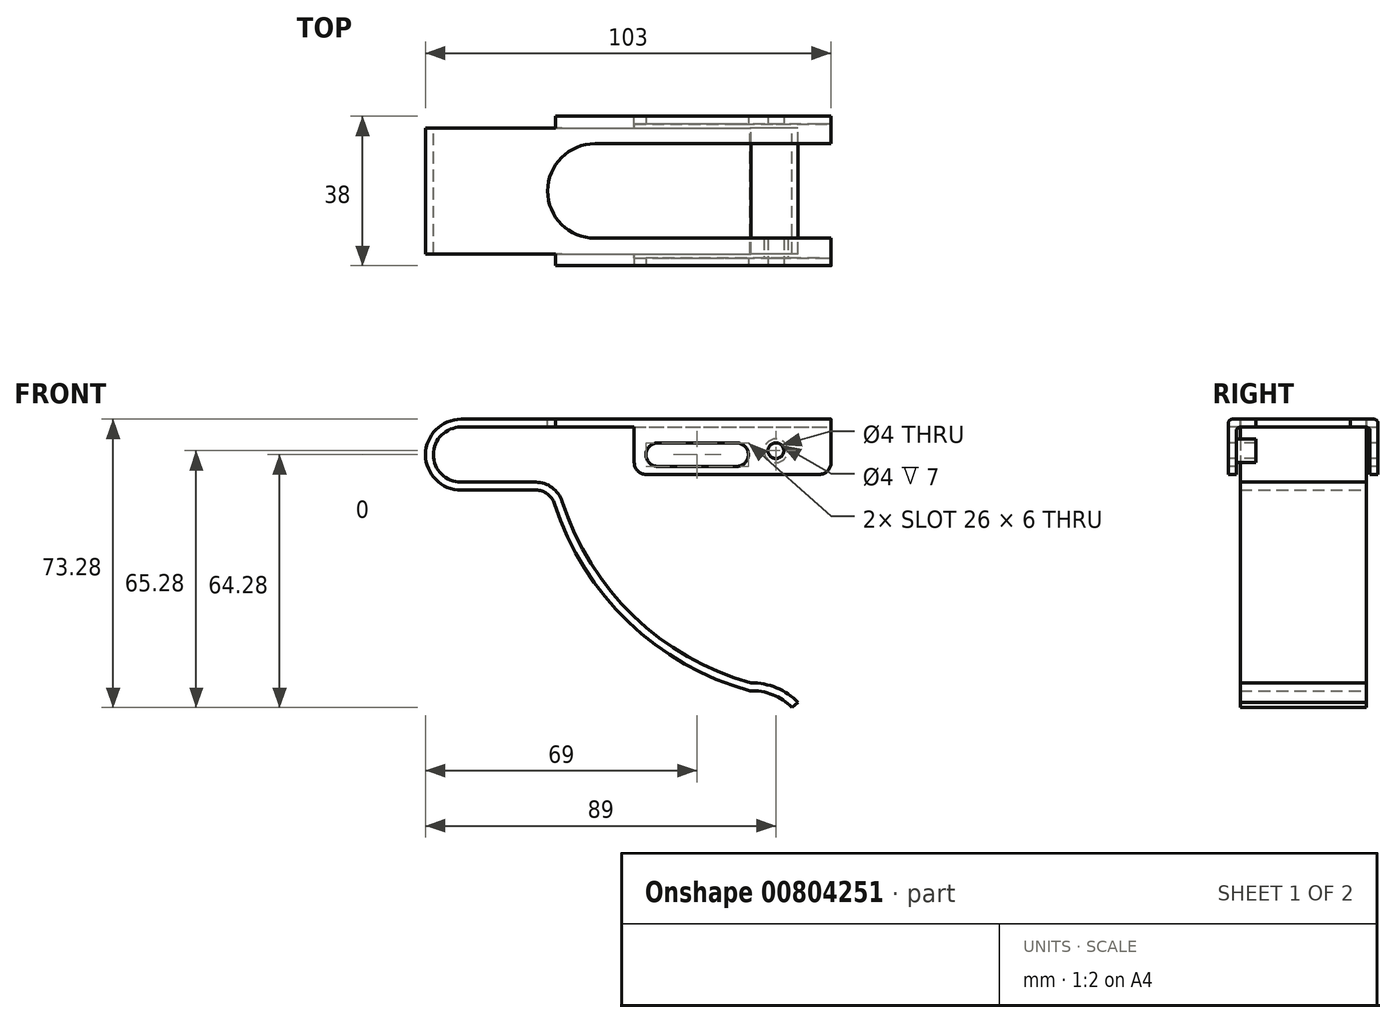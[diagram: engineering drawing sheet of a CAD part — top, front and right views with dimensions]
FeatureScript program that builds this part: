
annotation { "Feature Type Name" : "Feature", "Feature Type Description" : "" }
export const myFeature = defineFeature(function(context is Context, id is Id, definition is map)
    precondition{}
    {
        {
            var Q0;
            Q0=qCreatedBy(makeId("Front.planeOp"),FACE);
            var sketch = newSketch(context, id + "F0", { "sketchPlane" : qUnion([Q0])});
            skArc(sketch, "E0", {"start": v(0, 9) * mm, "mid": v(-9, 0) * mm, "end": v(0, -9) * mm});
            skLineSegment(sketch, "E1", {"start": v(0, 9) * mm, "end": v(94, 9) * mm});
            skLineSegment(sketch, "E2", {"start": v(0, -9) * mm, "end": v(19, -9) * mm});
            skArc(sketch, "E3", {"start": v(23.76, -12.48) * mm, "mid": v(42.54, -42.55) * mm, "end": v(73.4, -60) * mm});
            skArc(sketch, "E4", {"start": v(84.1, -64.28) * mm, "mid": v(79.2, -61) * mm, "end": v(73.4, -60) * mm});
            skPoint(sketch, "E5.visualSharp", {"position": v(22.75, -9) * mm});
            skArc(sketch, "E5.filletArc", {"start": v(23.76, -12.48) * mm, "mid": v(21.95, -9.96) * mm, "end": v(19, -9) * mm});
            skLineSegment(sketch, "E6.0", {"start": v(0, 7) * mm, "end": v(94, 7) * mm});
            skArc(sketch, "E6.1", {"start": v(0, 7) * mm, "mid": v(-7, 0) * mm, "end": v(0, -7) * mm});
            skArc(sketch, "E6.2", {"start": v(85.63, -63) * mm, "mid": v(80.16, -59.23) * mm, "end": v(73.63, -58) * mm});
            skArc(sketch, "E6.3", {"start": v(25.67, -11.87) * mm, "mid": v(43.82, -41) * mm, "end": v(73.63, -58) * mm});
            skArc(sketch, "E6.4", {"start": v(25.67, -11.87) * mm, "mid": v(23.13, -8.35) * mm, "end": v(19, -7) * mm});
            skLineSegment(sketch, "E6.5", {"start": v(0, -7) * mm, "end": v(19, -7) * mm});
            skLineSegment(sketch, "E7", {"start": v(94, 9) * mm, "end": v(94, 7) * mm});
            skLineSegment(sketch, "E8", {"start": v(85.63, -63) * mm, "end": v(84.1, -64.28) * mm});
            skSolve(sketch);
        }
        {
            var Q0;
            Q0 = qSketchRegion(id + "F0", true);
            extrude(context, id + "F1", {"entities" : qUnion([Q0]), "depth" : 16 * mm, "offsetDistance" : 25 * mm});
        }
        {
            var Q0;
            Q0=makeQuery(id+"F1.opExtrude","SWEPT_FACE",FACE,{"disambiguationData":[OSD([sQuery(id+"F0.wireOp",EDGE,"E1")])]});
            var sketch = newSketch(context, id + "F2", { "sketchPlane" : qUnion([Q0])});
            skLineSegment(sketch, "E9.bottom", {"start": v(94, -16) * mm, "end": v(24, -16) * mm});
            skLineSegment(sketch, "E9.top", {"start": v(94, -19) * mm, "end": v(24, -19) * mm});
            skLineSegment(sketch, "E9.left", {"start": v(94, -16) * mm, "end": v(94, -19) * mm});
            skLineSegment(sketch, "E9.right", {"start": v(24, -16) * mm, "end": v(24, -19) * mm});
            skSolve(sketch);
        }
        {
            var Q0;
            Q0=makeQuery(id+"F2.imprint","IMPRINT",FACE,{"disambiguationData":[TD([[makeQuery(id+"F2.imprint","IMPRINT",EDGE,{"derivedFrom":sQuery(id+"F2.wireOp",EDGE,"E9.bottom")}),-1.0]])]});
            extrude(context, id + "F3", {"entities" : qUnion([Q0]), "operationType" : NewBodyOperationType.ADD, "oppositeDirection" : true, "depth" : 2 * mm, "offsetDistance" : 25 * mm});
        }
        {
            var Q0;
            Q0=makeQuery(id+"F3.opExtrude","SWEPT_FACE",FACE,{"disambiguationData":[OSD([sQuery(id+"F2.wireOp",EDGE,"E9.top")])]});
            var sketch = newSketch(context, id + "F4", { "sketchPlane" : qUnion([Q0])});
            skLineSegment(sketch, "E10.bottom", {"start": v(94, 9) * mm, "end": v(44, 9) * mm});
            skLineSegment(sketch, "E10.top", {"start": v(94, -5) * mm, "end": v(44, -5) * mm});
            skLineSegment(sketch, "E10.left", {"start": v(94, 9) * mm, "end": v(94, -5) * mm});
            skLineSegment(sketch, "E10.right", {"start": v(44, 9) * mm, "end": v(44, -5) * mm});
            skSolve(sketch);
        }
        {
            var Q0;
            Q0 = qSketchRegion(id + "F4", true);
            extrude(context, id + "F5", {"entities" : qUnion([Q0]), "operationType" : NewBodyOperationType.ADD, "oppositeDirection" : true, "depth" : 2 * mm, "offsetDistance" : 25 * mm});
        }
        {
            var Q0;
            Q0=makeQuery(id+"F5.boolean.opBoolean","INTERSECT",EDGE,{"derivedFrom":[makeQuery(id+"F3.boolean.opBoolean","MERGE",FACE,{"derivedFrom":[makeQuery(id+"F1.opExtrude","SWEPT_FACE",FACE,{"disambiguationData":[OSD([sQuery(id+"F0.wireOp",EDGE,"E6.0")])]}),makeQuery(id+"F3.opExtrude","CAP_FACE",FACE,{"disambiguationData":[OSD([sQuery(id+"F2.wireOp",EDGE,"E9.bottom"),sQuery(id+"F2.wireOp",EDGE,"E9.top"),sQuery(id+"F2.wireOp",EDGE,"E9.left"),sQuery(id+"F2.wireOp",EDGE,"E9.right")])],"isStart":false})]}),makeQuery(id+"F5.opExtrude","CAP_FACE",FACE,{"disambiguationData":[OSD([sQuery(id+"F4.wireOp",EDGE,"E10.bottom"),sQuery(id+"F4.wireOp",EDGE,"E10.top"),sQuery(id+"F4.wireOp",EDGE,"E10.left"),sQuery(id+"F4.wireOp",EDGE,"E10.right")])],"isStart":false})]});
            var Q1;
            Q1=makeQuery(id+"F3.opExtrude","CAP_EDGE",EDGE,{"disambiguationData":[OSD([sQuery(id+"F2.wireOp",EDGE,"E9.top")])],"isStart":true});
            fillet(context, id + "F6", {"entities" : qUnion([Q0, Q1]), "radius" : 1 * mm, "tangentPropagation" : true, "allowEdgeOverflow" : false});
        }
        {
            var Q0;
            Q0=makeQuery(id+"F1.opExtrude","SWEPT_BODY",BODY,{"disambiguationData":[OSD([sQuery(id+"F0.wireOp",EDGE,"E0"),sQuery(id+"F0.wireOp",EDGE,"E1"),sQuery(id+"F0.wireOp",EDGE,"E2"),sQuery(id+"F0.wireOp",EDGE,"E3"),sQuery(id+"F0.wireOp",EDGE,"E4"),sQuery(id+"F0.wireOp",EDGE,"E5.filletArc"),sQuery(id+"F0.wireOp",EDGE,"E6.0"),sQuery(id+"F0.wireOp",EDGE,"E6.1"),sQuery(id+"F0.wireOp",EDGE,"E6.2"),sQuery(id+"F0.wireOp",EDGE,"E6.3"),sQuery(id+"F0.wireOp",EDGE,"E6.4"),sQuery(id+"F0.wireOp",EDGE,"E6.5"),sQuery(id+"F0.wireOp",EDGE,"E7"),sQuery(id+"F0.wireOp",EDGE,"E8")])]});
            var Q1;
            Q1=qCreatedBy(makeId("Front.planeOp"),FACE);
            mirror(context, id + "F7", {"operationType" : NewBodyOperationType.ADD, "entities" : qUnion([Q0]), "mirrorPlane" : qUnion([Q1])});
        }
        {
            var Q0;
            {var subQ0=makeQuery(id+"F3.boolean.opBoolean","MERGE",FACE,{"derivedFrom":[makeQuery(id+"F1.opExtrude","SWEPT_FACE",FACE,{"disambiguationData":[OSD([sQuery(id+"F0.wireOp",EDGE,"E1")])]}),makeQuery(id+"F3.opExtrude","CAP_FACE",FACE,{"disambiguationData":[OSD([sQuery(id+"F2.wireOp",EDGE,"E9.bottom"),sQuery(id+"F2.wireOp",EDGE,"E9.top"),sQuery(id+"F2.wireOp",EDGE,"E9.left"),sQuery(id+"F2.wireOp",EDGE,"E9.right")])],"isStart":true})]});Q0=makeQuery(id+"F7.boolean.opBoolean","MERGE",FACE,{"derivedFrom":[subQ0,makeQuery(id+"F7.opPattern","COPY",FACE,{"derivedFrom":subQ0,"instanceName":"1"})]});}
            var sketch = newSketch(context, id + "F8", { "sketchPlane" : qUnion([Q0])});
            skArc(sketch, "E11", {"start": v(34, 12) * mm, "mid": v(22, 0) * mm, "end": v(34, -12) * mm});
            skLineSegment(sketch, "E12", {"start": v(34, 12) * mm, "end": v(94, 12) * mm});
            skLineSegment(sketch, "E13", {"start": v(34, -12) * mm, "end": v(94, -12) * mm});
            skLineSegment(sketch, "E14", {"start": v(94, -12) * mm, "end": v(94, 12) * mm});
            skSolve(sketch);
        }
        {
            var Q0;
            Q0 = qSketchRegion(id + "F8", true);
            extrude(context, id + "F9", {"entities" : qUnion([Q0]), "operationType" : NewBodyOperationType.REMOVE, "oppositeDirection" : true, "depth" : 2 * mm, "offsetDistance" : 25 * mm});
        }
        {
            var Q0;
            Q0=makeQuery(id+"F5.boolean.opBoolean","MERGE",FACE,{"derivedFrom":[makeQuery(id+"F3.opExtrude","SWEPT_FACE",FACE,{"disambiguationData":[OSD([sQuery(id+"F2.wireOp",EDGE,"E9.top")])]}),makeQuery(id+"F5.opExtrude","CAP_FACE",FACE,{"disambiguationData":[OSD([sQuery(id+"F4.wireOp",EDGE,"E10.bottom"),sQuery(id+"F4.wireOp",EDGE,"E10.top"),sQuery(id+"F4.wireOp",EDGE,"E10.left"),sQuery(id+"F4.wireOp",EDGE,"E10.right")])],"isStart":true})]});
            var sketch = newSketch(context, id + "F10", { "sketchPlane" : qUnion([Q0])});
            skLineSegment(sketch, "E15", {"start": v(50, 0) * mm, "end": v(70, 0) * mm});
            skArc(sketch, "E16.0.startCap", {"start": v(50, -3) * mm, "mid": v(47, 0) * mm, "end": v(50, 3) * mm});
            skArc(sketch, "E16.0.endCap", {"start": v(70, 3) * mm, "mid": v(73, 0) * mm, "end": v(70, -3) * mm});
            skLineSegment(sketch, "E16.0.left", {"start": v(50, 3) * mm, "end": v(70, 3) * mm});
            skLineSegment(sketch, "E16.0.right", {"start": v(50, -3) * mm, "end": v(70, -3) * mm});
            skSolve(sketch);
        }
        {
            var Q0;
            Q0 = qSketchRegion(id + "F10", true);
            extrude(context, id + "F11", {"entities" : qUnion([Q0]), "operationType" : NewBodyOperationType.REMOVE, "endBound" : BoundingType.THROUGH_ALL, "oppositeDirection" : true, "depth" : 25 * mm, "offsetDistance" : 25 * mm});
        }
        {
            var Q0;
            Q0=makeQuery(id+"F5.boolean.opBoolean","MERGE",FACE,{"derivedFrom":[makeQuery(id+"F3.opExtrude","SWEPT_FACE",FACE,{"disambiguationData":[OSD([sQuery(id+"F2.wireOp",EDGE,"E9.top")])]}),makeQuery(id+"F5.opExtrude","CAP_FACE",FACE,{"disambiguationData":[OSD([sQuery(id+"F4.wireOp",EDGE,"E10.bottom"),sQuery(id+"F4.wireOp",EDGE,"E10.top"),sQuery(id+"F4.wireOp",EDGE,"E10.left"),sQuery(id+"F4.wireOp",EDGE,"E10.right")])],"isStart":true})]});
            var sketch = newSketch(context, id + "F12", { "sketchPlane" : qUnion([Q0])});
            skPoint(sketch, "E17", {"position": v(80, 1) * mm});
            skSolve(sketch);
        }
        {
            var Q0;
            Q0=sQuery(id+"F12.wireOp",VERTEX,"E17");
            var Q1;
            Q1=makeQuery(id+"F1.opExtrude","SWEPT_BODY",BODY,{"disambiguationData":[OSD([sQuery(id+"F0.wireOp",EDGE,"E0"),sQuery(id+"F0.wireOp",EDGE,"E1"),sQuery(id+"F0.wireOp",EDGE,"E2"),sQuery(id+"F0.wireOp",EDGE,"E3"),sQuery(id+"F0.wireOp",EDGE,"E4"),sQuery(id+"F0.wireOp",EDGE,"E5.filletArc"),sQuery(id+"F0.wireOp",EDGE,"E6.0"),sQuery(id+"F0.wireOp",EDGE,"E6.1"),sQuery(id+"F0.wireOp",EDGE,"E6.2"),sQuery(id+"F0.wireOp",EDGE,"E6.3"),sQuery(id+"F0.wireOp",EDGE,"E6.4"),sQuery(id+"F0.wireOp",EDGE,"E6.5"),sQuery(id+"F0.wireOp",EDGE,"E7"),sQuery(id+"F0.wireOp",EDGE,"E8")])]});
            hole(context, id + "F13", {"style" : HoleStyle.SIMPLE, "endStyle" : HoleEndStyle.THROUGH, "holeDiameter" : 4 * mm, "majorDiameter" : 5 * mm, "isTappedThrough" : true, "tappedDepth" : 12 * mm, "tapClearance" : 3, "locations" : qUnion([Q0]), "scope" : qUnion([Q1])});
        }
        {
            var Q0;
            Q0=makeQuery(id+"F5.opExtrude","CAP_FACE",FACE,{"disambiguationData":[OSD([sQuery(id+"F4.wireOp",EDGE,"E10.bottom"),sQuery(id+"F4.wireOp",EDGE,"E10.top"),sQuery(id+"F4.wireOp",EDGE,"E10.left"),sQuery(id+"F4.wireOp",EDGE,"E10.right")])],"isStart":false});
            var sketch = newSketch(context, id + "F14", { "sketchPlane" : qUnion([Q0])});
            skCircle(sketch, "E18.0", {"center": v(-80, 1) * mm, "radius": 2 * mm});
            skCircle(sketch, "E19.0", {"center": v(-80, 1) * mm, "radius": 3 * mm});
            skSolve(sketch);
        }
        {
            var Q0;
            Q0=makeQuery(id+"F14.imprint","IMPRINT",FACE,{"disambiguationData":[TD([[makeQuery(id+"F14.imprint","IMPRINT",EDGE,{"derivedFrom":sQuery(id+"F14.wireOp",EDGE,"E18.0")}),-1.0]])]});
            extrude(context, id + "F15", {"entities" : qUnion([Q0]), "operationType" : NewBodyOperationType.ADD, "depth" : 5 * mm, "offsetDistance" : 25 * mm});
        }
        {
            var Q0;
            Q0=makeQuery(id+"F5.opExtrude","SWEPT_EDGE",EDGE,{"disambiguationData":[OSD([sQuery(id+"F4.wireOp",EDGE,"E10.top"),sQuery(id+"F4.wireOp",EDGE,"E10.left")])]});
            var Q1;
            Q1=makeQuery(id+"F7.opPattern","COPY",EDGE,{"derivedFrom":makeQuery(id+"F5.opExtrude","SWEPT_EDGE",EDGE,{"disambiguationData":[OSD([sQuery(id+"F4.wireOp",EDGE,"E10.top"),sQuery(id+"F4.wireOp",EDGE,"E10.left")])]}),"instanceName":"1"});
            var Q2;
            Q2=makeQuery(id+"F7.opPattern","COPY",EDGE,{"derivedFrom":makeQuery(id+"F5.opExtrude","SWEPT_EDGE",EDGE,{"disambiguationData":[OSD([sQuery(id+"F4.wireOp",EDGE,"E10.top"),sQuery(id+"F4.wireOp",EDGE,"E10.right")])]}),"instanceName":"1"});
            var Q3;
            Q3=makeQuery(id+"F5.opExtrude","SWEPT_EDGE",EDGE,{"disambiguationData":[OSD([sQuery(id+"F4.wireOp",EDGE,"E10.top"),sQuery(id+"F4.wireOp",EDGE,"E10.right")])]});
            fillet(context, id + "F16", {"entities" : qUnion([Q0, Q1, Q2, Q3]), "radius" : 3 * mm, "tangentPropagation" : true, "allowEdgeOverflow" : false});
        }
    });
